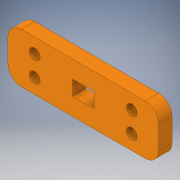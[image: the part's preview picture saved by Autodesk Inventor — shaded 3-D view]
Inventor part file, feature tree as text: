
AUTODESK INVENTOR PART (.ipt)
format: ipt  version: 2017 (Build 210142000, 142)  size: 137,216 bytes
history: native  units: in
note: dims shown in document units (in); Inventor stores cm internally (conversion verified against a paired STEP export)
features: sketch x3, extrude x2, hole x1, plane x1, mirror x1, fillet x1
ambient origin geometry x8: Origin, YZ Plane, XZ Plane, XY Plane, X Axis, Y Axis, Z Axis, Center Point
bodies: Solid1 (feature_tree)
feature tree (9):
  extrude  "Extrusion1"  Depth=0.93in
  hole  "Hole2"  [1 undecoded]
  plane  "Work Plane1"
  mirror  "Mirror1"
  extrude  "Extrusion2"  Depth=0.25in
  fillet  "Fillet1"  Radius=0.501in
  sketch  "Sketch1"  dims[d0=2.813in d1=0.93in]
  sketch  "Sketch3"  dims[d2=0.25in d3=0.0in d15=0.275in]
  sketch  "Sketch4"  dims[d16=0.275in d17=0.501in d18=0.501in d19=0.2in d20=0.75in d21=0.375in d22=0.25in d23=0.5635in d24=1.0in d25=0.8108in d26=0.4in d27=0.28in d28=2.813in d29=1.2065in d30=0.325in d31=0.93in d32=0.25in d33=0.0in d34=0.25in]
note: 1 required parameter value undecoded (feature->parameter linkage not recoverable at this tier; creation-order binding heuristic only, values carry confidence <= 0.55)
